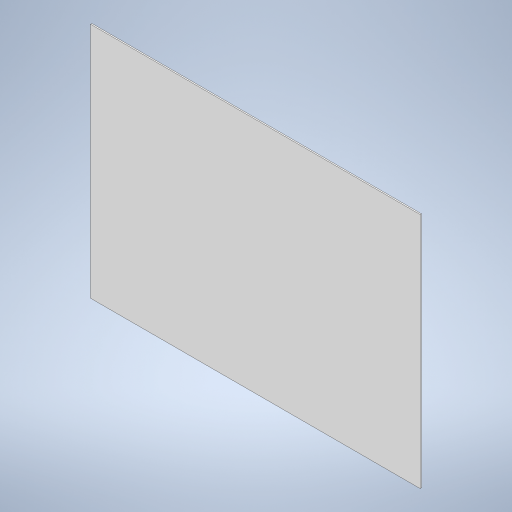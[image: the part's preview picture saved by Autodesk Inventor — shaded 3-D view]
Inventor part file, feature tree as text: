
AUTODESK INVENTOR PART (.ipt)
format: ipt  version: 2023 (Build 270158000, 158)  size: 407,040 bytes
history: native  units: mm
features: other x2, sketch x2, extrude x1, plane x1
ambient origin geometry x8: Origin, YZ Plane, XZ Plane, XY Plane, X Axis, Y Axis, Z Axis, Center Point
bodies: Solid1 (feature_tree)
feature tree (6):
  extrude  "Extrusion1"  Depth=540.0mm
  plane  "Work Plane2"
  other  "Decal1"
  sketch  "Sketch1"  dims[d0=750.0mm d1=540.0mm]
  sketch  "Sketch3"  dims[d2=3.0mm d3=0.0mm d13=0.0mm d28=0.0mm d29=750.0mm d30=750.0mm d35=540.0mm d38=750.0mm d39=105.0mm]
  other  "Image4"
